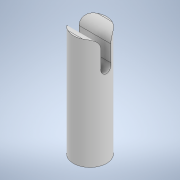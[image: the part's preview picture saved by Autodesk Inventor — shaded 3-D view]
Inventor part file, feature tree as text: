
AUTODESK INVENTOR PART (.ipt)
format: ipt  version: 2021.1 (Build 251245010, 245A)  size: 149,504 bytes
history: native  units: in
note: dims shown in document units (in); Inventor stores cm internally (conversion verified against a paired STEP export)
features: sketch x2, revolve x1, plane x1, extrude x1, fillet x1
ambient origin geometry x8: Origin, YZ Plane, XZ Plane, XY Plane, X Axis, Y Axis, Z Axis, Center Point
bodies: Body1 (feature_tree)
feature tree (6):
  revolve  "Revolution2"  [1 undecoded]
  plane  "Work Plane1"
  extrude  "Extrusion1"  Depth=0.125in
  fillet  "Fillet1"  Radius=0.35in
  sketch  "Sketch2"  dims[d6=0.21in d7=0.16in]
  sketch  "Sketch3"  dims[d8=0.55in d9=0.0625in d10=0.35in d14=0.0312in d16=0.5in d17=90.0deg d18=0.13in d19=0.35in d21=0.0625in d22=0.0in d23=0.0in d24=0.125in]
note: 1 required parameter value undecoded (feature->parameter linkage not recoverable at this tier; creation-order binding heuristic only, values carry confidence <= 0.55)
